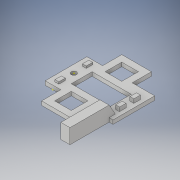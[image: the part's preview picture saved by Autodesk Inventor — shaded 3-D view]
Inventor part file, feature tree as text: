
AUTODESK INVENTOR PART (.ipt)
format: ipt  version: 2018 (Build 220112000, 112)  size: 242,176 bytes
history: native  units: in
note: dims shown in document units (in); Inventor stores cm internally (conversion verified against a paired STEP export)
features: sketch x14, extrude x7, draft x1
ambient origin geometry x8: Origin, YZ Plane, XZ Plane, XY Plane, X Axis, Y Axis, Z Axis, Center Point
bodies: Solid1 (feature_tree)
feature tree (22):
  sketch  "Sketch1"  dims[d0=0.1575in d1=0.5906in]
  sketch  "Sketch2"  dims[d2=0.6299in d3=0.2362in]
  sketch  "Sketch3"  dims[d4=0.1181in d5=0.1969in]
  sketch  "Sketch4"  dims[d6=0.315in d7=0.315in]
  sketch  "Sketch5"  dims[d11=0.9843in d12=0.4724in]
  sketch  "Sketch6"  dims[d13=0.8957in d14=0.8957in]
  extrude  "Extrusion1"  Depth=0.1575in
  sketch  "Sketch7"  dims[d15=0.0in d16=0.1181in]
  extrude  "Extrusion2"  Depth=0.2362in
  extrude  "Extrusion3"  Depth=0.1969in
  extrude  "Extrusion4"  Depth=0.315in
  extrude  "Extrusion5"  Depth=0.4724in
  extrude  "Extrusion6"  Depth=0.8957in
  sketch  "Sketch12"  dims[d26=0.1181in d27=0.0in]
  sketch  "Sketch13"  dims[d28=0.502in]
  draft  "FaceDraft1"
  extrude  "Extrusion7"  Depth=0.1181in
  sketch  "Sketch8"  dims[d17=0.1969in]
  sketch  "Sketch9"  dims[d21=0.1181in d22=0.0in]
  sketch  "Sketch10"  dims[d23=0.1181in d24=0.0in]
  sketch  "Sketch11"  dims[d25=0.3937in]
  sketch  "Sketch14"  dims[d29=0.502in d30=0.1969in d31=0.1181in d32=0.0in d33=0.1181in d34=0.1969in d35=0.1575in d36=0.1181in d37=0.0in d38=0.2756in d39=1.1811in d40=0.3287in d41=0.1181in d42=0.0in d43=0.0in d44=30.0deg d46=0.502in d47=0.502in d48=0.3287in d49=0.0in]
